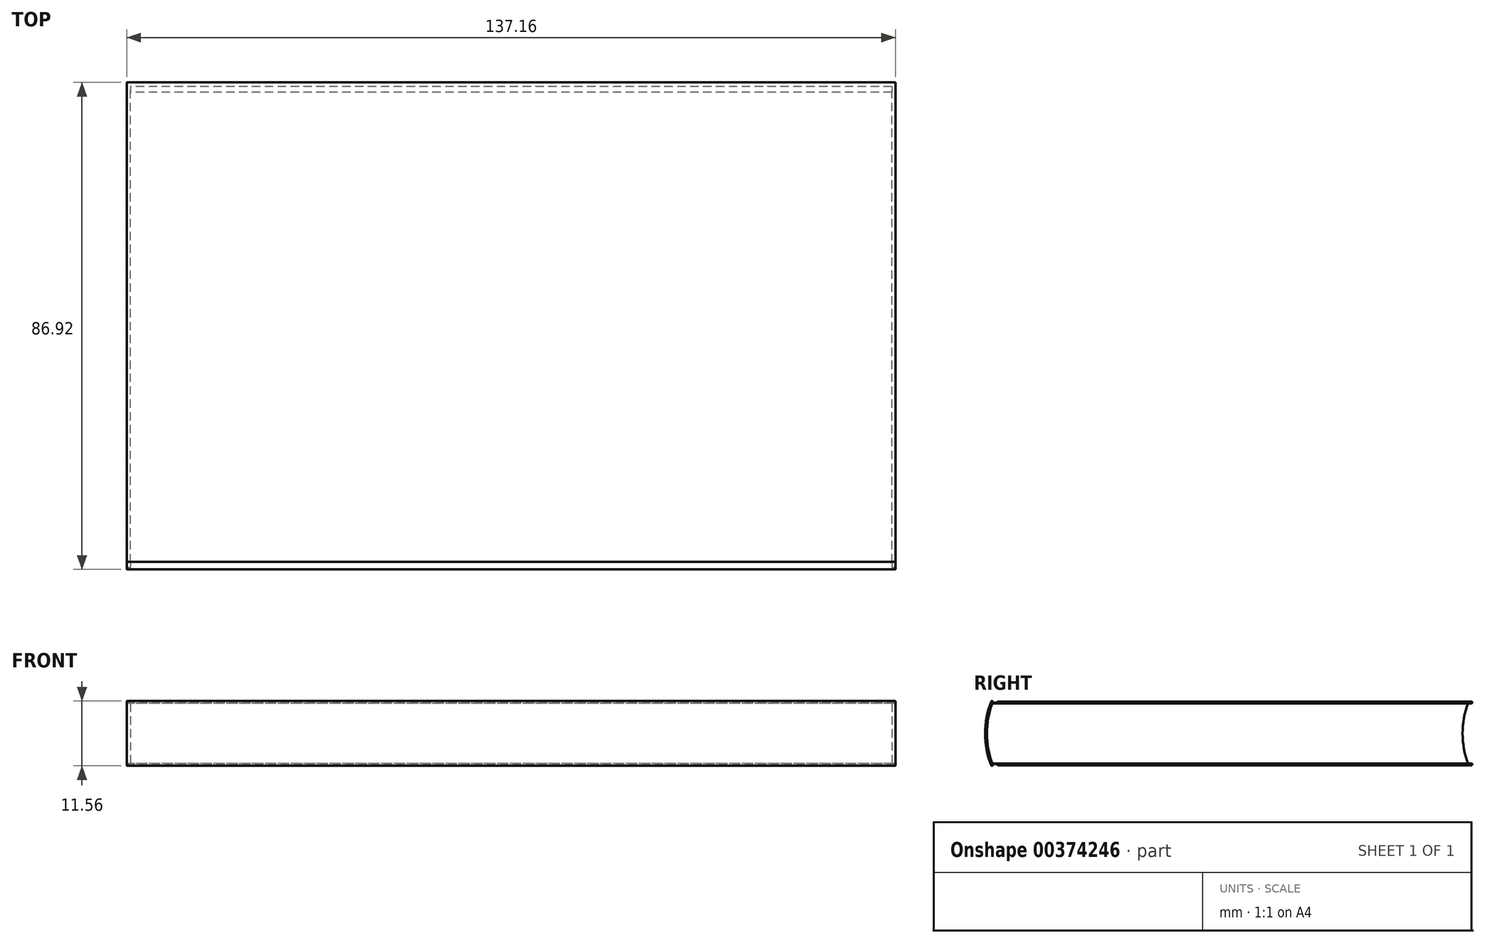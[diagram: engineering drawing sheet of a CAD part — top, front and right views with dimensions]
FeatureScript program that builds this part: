
annotation { "Feature Type Name" : "Feature", "Feature Type Description" : "" }
export const myFeature = defineFeature(function(context is Context, id is Id, definition is map)
    precondition{}
    {
        {
            var Q0;
            Q0=qCreatedBy(makeId("Right.planeOp"),FACE);
            var sketch = newSketch(context, id + "F0", { "sketchPlane" : qUnion([Q0])});
            skLineSegment(sketch, "E0", {"start": v(-62.81, 0) * mm, "end": v(107.73, 0) * mm});
            skArc(sketch, "E1", {"start": v(-62.81, 0) * mm, "mid": v(-63.25, 0.21) * mm, "end": v(-63.7, 0) * mm});
            skArc(sketch, "E2", {"start": v(-64, 0) * mm, "mid": v(-63.85, -0.1) * mm, "end": v(-63.7, 0) * mm});
            skLineSegment(sketch, "E3", {"start": v(-64, 0) * mm, "end": v(-64, 28.97) * mm, "construction": true});
            skLineSegment(sketch, "E4", {"start": v(-64, 28.97) * mm, "end": v(-61.08, 28.97) * mm, "construction": true});
            skLineSegment(sketch, "E5.MirrorCS", {"start": v(-64, 57.95) * mm, "end": v(-64, 28.97) * mm, "construction": true});
            skLineSegment(sketch, "E6.MirrorCS", {"start": v(-62.81, 57.95) * mm, "end": v(107.73, 57.95) * mm});
            skArc(sketch, "E7.MirrorCS", {"start": v(-64, 57.95) * mm, "mid": v(-63.85, 58.05) * mm, "end": v(-63.7, 57.95) * mm});
            skArc(sketch, "E8.MirrorCS", {"start": v(-62.81, 57.95) * mm, "mid": v(-63.25, 57.73) * mm, "end": v(-63.7, 57.95) * mm});
            skArc(sketch, "E9", {"start": v(-64, 57.95) * mm, "mid": v(-69.44, 28.97) * mm, "end": v(-64, 0) * mm});
            skLineSegment(sketch, "E10", {"start": v(-63.85, 0.06) * mm, "end": v(-64, 0) * mm, "construction": true});
            skLineSegment(sketch, "E11", {"start": v(-64, 0) * mm, "end": v(-65.18, 3.02) * mm, "construction": true});
            skLineSegment(sketch, "E12", {"start": v(-64, 0) * mm, "end": v(-63.7, 0) * mm, "construction": true});
            skLineSegment(sketch, "E13", {"start": v(107.73, 0) * mm, "end": v(107.73, 0.31) * mm, "construction": true});
            skArc(sketch, "E14", {"start": v(107.73, 0) * mm, "mid": v(107.89, 0.16) * mm, "end": v(107.73, 0.31) * mm});
            skArc(sketch, "E15.MirrorCS", {"start": v(107.73, 57.95) * mm, "mid": v(107.89, 57.79) * mm, "end": v(107.73, 57.63) * mm});
            skLineSegment(sketch, "E16", {"start": v(107.73, 0.31) * mm, "end": v(-63.8, 0.31) * mm});
            skLineSegment(sketch, "E17", {"start": v(-44.13, 0) * mm, "end": v(-44.13, 0.31) * mm, "construction": true});
            skLineSegment(sketch, "E18", {"start": v(-63.8, 0.31) * mm, "end": v(-64.08, 0.2) * mm, "construction": true});
            skLineSegment(sketch, "E19.MirrorCS", {"start": v(107.73, 57.63) * mm, "end": v(-63.8, 57.63) * mm});
            skArc(sketch, "E20", {"start": v(-63.8, 57.63) * mm, "mid": v(-69.13, 28.97) * mm, "end": v(-63.8, 0.31) * mm});
            skLineSegment(sketch, "E21", {"start": v(-69.13, 28.97) * mm, "end": v(-69.44, 28.97) * mm, "construction": true});
            skLineSegment(sketch, "E22.bottom", {"start": v(-63.8, 57.63) * mm, "end": v(107.2, 57.63) * mm});
            skLineSegment(sketch, "E22.top", {"start": v(-63.8, 0.31) * mm, "end": v(107.2, 0.31) * mm});
            skLineSegment(sketch, "E22.left", {"start": v(-63.8, 57.63) * mm, "end": v(-63.8, 0.31) * mm});
            skLineSegment(sketch, "E22.right", {"start": v(107.2, 57.63) * mm, "end": v(107.2, 0.31) * mm});
            skSolve(sketch);
        }
        {
            var Q0;
            Q0=qCreatedBy(makeId("Right.planeOp"),FACE);
            var sketch = newSketch(context, id + "F1", { "sketchPlane" : qUnion([Q0])});
            skLineSegment(sketch, "E23", {"start": v(-62.81, 0) * mm, "end": v(21.7, 0) * mm});
            skLineSegment(sketch, "E24", {"start": v(-62.81, 0) * mm, "end": v(-62.81, 0) * mm});
            skArc(sketch, "E25", {"start": v(-62.81, 0) * mm, "mid": v(-63.25, 0.21) * mm, "end": v(-63.7, 0) * mm});
            skArc(sketch, "E26", {"start": v(-64, 0) * mm, "mid": v(-63.85, -0.1) * mm, "end": v(-63.7, 0) * mm});
            skLineSegment(sketch, "E27", {"start": v(21.7, 0) * mm, "end": v(21.7, 0) * mm});
            skLineSegment(sketch, "E28", {"start": v(-64, 0) * mm, "end": v(-64, 5.67) * mm, "construction": true});
            skLineSegment(sketch, "E29", {"start": v(-64, 5.67) * mm, "end": v(-60.85, 5.67) * mm, "construction": true});
            skLineSegment(sketch, "E30.MirrorCS", {"start": v(-64, 11.34) * mm, "end": v(-64, 5.67) * mm, "construction": true});
            skArc(sketch, "E31.MirrorCS", {"start": v(-64, 11.34) * mm, "mid": v(-63.85, 11.45) * mm, "end": v(-63.7, 11.34) * mm});
            skArc(sketch, "E32.MirrorCS", {"start": v(-62.81, 11.34) * mm, "mid": v(-63.25, 11.13) * mm, "end": v(-63.7, 11.34) * mm});
            skLineSegment(sketch, "E33.MirrorCS", {"start": v(-62.81, 11.34) * mm, "end": v(21.7, 11.34) * mm});
            skLineSegment(sketch, "E34.MirrorCS", {"start": v(21.7, 11.34) * mm, "end": v(21.7, 11.34) * mm});
            skLineSegment(sketch, "E35.0", {"start": v(-64, 0) * mm, "end": v(-65.18, 3.02) * mm, "construction": true});
            skArc(sketch, "E36", {"start": v(-64, 11.34) * mm, "mid": v(-65.07, 5.67) * mm, "end": v(-64, 0) * mm});
            skArc(sketch, "E37", {"start": v(-63.8, 11.03) * mm, "mid": v(-64.77, 5.67) * mm, "end": v(-63.8, 0.31) * mm});
            skLineSegment(sketch, "E38", {"start": v(-64.77, 5.67) * mm, "end": v(-65.07, 5.67) * mm, "construction": true});
            skLineSegment(sketch, "E39", {"start": v(-64.06, 1) * mm, "end": v(-63.8, 0.31) * mm, "construction": true});
            skLineSegment(sketch, "E40", {"start": v(-64, 0) * mm, "end": v(-63.72, 0.1) * mm, "construction": true});
            skLineSegment(sketch, "E41", {"start": v(21.7, 0.31) * mm, "end": v(21.7, 0) * mm, "construction": true});
            skArc(sketch, "E42", {"start": v(21.7, 0) * mm, "mid": v(21.85, 0.16) * mm, "end": v(21.7, 0.31) * mm});
            skLineSegment(sketch, "E43", {"start": v(-63.8, 0.31) * mm, "end": v(21.7, 0.31) * mm});
            skLineSegment(sketch, "E44.MirrorCS", {"start": v(-63.8, 11.03) * mm, "end": v(21.7, 11.03) * mm});
            skArc(sketch, "E45.MirrorCS", {"start": v(21.7, 11.34) * mm, "mid": v(21.85, 11.19) * mm, "end": v(21.7, 11.03) * mm});
            skLineSegment(sketch, "E46", {"start": v(-63.8, 11.03) * mm, "end": v(-63.8, 0.31) * mm, "construction": true});
            skLineSegment(sketch, "E47", {"start": v(-63.8, 5.67) * mm, "end": v(-64.77, 5.67) * mm, "construction": true});
            skLineSegment(sketch, "E48", {"start": v(21.09, 11.03) * mm, "end": v(21.09, 0.31) * mm, "construction": true});
            skLineSegment(sketch, "E49", {"start": v(21.09, 5.67) * mm, "end": v(20.12, 5.67) * mm, "construction": true});
            skArc(sketch, "E50", {"start": v(21.09, 11.03) * mm, "mid": v(20.12, 5.67) * mm, "end": v(21.09, 0.31) * mm});
            skSolve(sketch);
        }
        {
            var Q0;
            Q0=makeQuery(id+"F1.imprint","IMPRINT",FACE,{"disambiguationData":[TD([[makeQuery(id+"F1.imprint","IMPRINT",EDGE,{"derivedFrom":sQuery(id+"F1.wireOp",EDGE,"E23")}),1.0]])]});
            extrude(context, id + "F2", {"entities" : qUnion([Q0]), "endBound" : BoundingType.SYMMETRIC, "depth" : 137.16 * mm});
        }
        {
            var Q0;
            Q0=makeQuery(id+"F2.opExtrude","CAP_EDGE",EDGE,{"disambiguationData":[OSD([sQuery(id+"F1.wireOp",EDGE,"E36")])],"isStart":false});
            var Q1;
            Q1=makeQuery(id+"F2.opExtrude","CAP_EDGE",EDGE,{"disambiguationData":[OSD([sQuery(id+"F1.wireOp",EDGE,"E37")])],"isStart":false});
            var Q2;
            Q2=makeQuery(id+"F2.opExtrude","CAP_EDGE",EDGE,{"disambiguationData":[OSD([sQuery(id+"F1.wireOp",EDGE,"E31.MirrorCS")])],"isStart":false});
            var Q3;
            Q3=makeQuery(id+"F2.opExtrude","CAP_EDGE",EDGE,{"disambiguationData":[OSD([sQuery(id+"F1.wireOp",EDGE,"E32.MirrorCS")])],"isStart":false});
            var Q4;
            Q4=makeQuery(id+"F2.opExtrude","CAP_EDGE",EDGE,{"disambiguationData":[OSD([sQuery(id+"F1.wireOp",EDGE,"142f4ce0-e9b1-4b00-a699-831a67d240180.MirrorCS"),sQuery(id+"F1.wireOp",EDGE,"xczyOIpz-feBP-V8Je-0c5D-2grpSOWJgWFw.top")])],"isStart":false});
            var Q5;
            Q5=makeQuery(id+"F2.opExtrude","CAP_EDGE",EDGE,{"disambiguationData":[OSD([sQuery(id+"F1.wireOp",EDGE,"E33.MirrorCS")])],"isStart":false});
            var Q6;
            Q6=makeQuery(id+"F2.opExtrude","CAP_EDGE",EDGE,{"disambiguationData":[OSD([sQuery(id+"F1.wireOp",EDGE,"E34.MirrorCS")])],"isStart":false});
            var Q7;
            Q7=makeQuery(id+"F2.opExtrude","CAP_EDGE",EDGE,{"disambiguationData":[OSD([sQuery(id+"F1.wireOp",EDGE,"E26")])],"isStart":false});
            var Q8;
            Q8=makeQuery(id+"F2.opExtrude","CAP_EDGE",EDGE,{"disambiguationData":[OSD([sQuery(id+"F1.wireOp",EDGE,"E25")])],"isStart":false});
            var Q9;
            Q9=makeQuery(id+"F2.opExtrude","CAP_EDGE",EDGE,{"disambiguationData":[OSD([sQuery(id+"F1.wireOp",EDGE,"E23")])],"isStart":false});
            var Q10;
            Q10=makeQuery(id+"F2.opExtrude","CAP_EDGE",EDGE,{"disambiguationData":[OSD([sQuery(id+"F1.wireOp",EDGE,"r9oz5I4B-ejXC-MW1O-M8zh-qOg59PADHznW"),sQuery(id+"F1.wireOp",EDGE,"xczyOIpz-feBP-V8Je-0c5D-2grpSOWJgWFw.bottom")])],"isStart":false});
            var Q11;
            Q11=makeQuery(id+"F2.opExtrude","CAP_EDGE",EDGE,{"disambiguationData":[OSD([sQuery(id+"F1.wireOp",EDGE,"E27")])],"isStart":false});
            fillet(context, id + "F3", {"entities" : qUnion([Q0, Q1, Q2, Q3, Q4, Q5, Q6, Q7, Q8, Q9, Q10, Q11]), "radius" : 0.06 * mm, "tangentPropagation" : true, "allowEdgeOverflow" : false});
        }
        {
            var Q0;
            Q0=makeQuery(id+"F2.opExtrude","CAP_EDGE",EDGE,{"disambiguationData":[OSD([sQuery(id+"F1.wireOp",EDGE,"E34.MirrorCS")])],"isStart":true});
            var Q1;
            Q1=makeQuery(id+"F2.opExtrude","CAP_EDGE",EDGE,{"disambiguationData":[OSD([sQuery(id+"F1.wireOp",EDGE,"E33.MirrorCS")])],"isStart":true});
            var Q2;
            Q2=makeQuery(id+"F2.opExtrude","CAP_EDGE",EDGE,{"disambiguationData":[OSD([sQuery(id+"F1.wireOp",EDGE,"142f4ce0-e9b1-4b00-a699-831a67d240180.MirrorCS"),sQuery(id+"F1.wireOp",EDGE,"xczyOIpz-feBP-V8Je-0c5D-2grpSOWJgWFw.top")])],"isStart":true});
            var Q3;
            Q3=makeQuery(id+"F2.opExtrude","CAP_EDGE",EDGE,{"disambiguationData":[OSD([sQuery(id+"F1.wireOp",EDGE,"E32.MirrorCS")])],"isStart":true});
            var Q4;
            Q4=makeQuery(id+"F2.opExtrude","CAP_EDGE",EDGE,{"disambiguationData":[OSD([sQuery(id+"F1.wireOp",EDGE,"E31.MirrorCS")])],"isStart":true});
            var Q5;
            Q5=makeQuery(id+"F2.opExtrude","CAP_EDGE",EDGE,{"disambiguationData":[OSD([sQuery(id+"F1.wireOp",EDGE,"E36")])],"isStart":true});
            var Q6;
            Q6=makeQuery(id+"F2.opExtrude","CAP_EDGE",EDGE,{"disambiguationData":[OSD([sQuery(id+"F1.wireOp",EDGE,"E37")])],"isStart":true});
            var Q7;
            Q7=makeQuery(id+"F2.opExtrude","CAP_EDGE",EDGE,{"disambiguationData":[OSD([sQuery(id+"F1.wireOp",EDGE,"E26")])],"isStart":true});
            var Q8;
            Q8=makeQuery(id+"F2.opExtrude","CAP_EDGE",EDGE,{"disambiguationData":[OSD([sQuery(id+"F1.wireOp",EDGE,"E25")])],"isStart":true});
            var Q9;
            Q9=makeQuery(id+"F2.opExtrude","CAP_EDGE",EDGE,{"disambiguationData":[OSD([sQuery(id+"F1.wireOp",EDGE,"r9oz5I4B-ejXC-MW1O-M8zh-qOg59PADHznW"),sQuery(id+"F1.wireOp",EDGE,"xczyOIpz-feBP-V8Je-0c5D-2grpSOWJgWFw.bottom")])],"isStart":true});
            var Q10;
            Q10=makeQuery(id+"F2.opExtrude","CAP_EDGE",EDGE,{"disambiguationData":[OSD([sQuery(id+"F1.wireOp",EDGE,"E23")])],"isStart":true});
            var Q11;
            Q11=makeQuery(id+"F2.opExtrude","CAP_EDGE",EDGE,{"disambiguationData":[OSD([sQuery(id+"F1.wireOp",EDGE,"E27")])],"isStart":true});
            fillet(context, id + "F4", {"entities" : qUnion([Q0, Q1, Q2, Q3, Q4, Q5, Q6, Q7, Q8, Q9, Q10, Q11]), "radius" : 0.06 * mm, "tangentPropagation" : true, "allowEdgeOverflow" : false});
        }
        {
            var Q0;
            Q0=makeQuery(id+"F2.opExtrude","SWEPT_EDGE",EDGE,{"disambiguationData":[OSD([sQuery(id+"F1.wireOp",EDGE,"E32.MirrorCS"),sQuery(id+"F1.wireOp",EDGE,"E33.MirrorCS")])]});
            var Q1;
            Q1=makeQuery(id+"F4.opFillet","BLEND_EDGE",EDGE,{"blendedFrom":[makeQuery(id+"F2.opExtrude","CAP_EDGE",EDGE,{"disambiguationData":[OSD([sQuery(id+"F1.wireOp",EDGE,"E32.MirrorCS")])],"isStart":true}),makeQuery(id+"F2.opExtrude","CAP_EDGE",EDGE,{"disambiguationData":[OSD([sQuery(id+"F1.wireOp",EDGE,"E33.MirrorCS")])],"isStart":true})],"blendedInto":[]});
            var Q2;
            Q2=makeQuery(id+"F3.opFillet","BLEND_EDGE",EDGE,{"blendedFrom":[makeQuery(id+"F2.opExtrude","CAP_EDGE",EDGE,{"disambiguationData":[OSD([sQuery(id+"F1.wireOp",EDGE,"E32.MirrorCS")])],"isStart":false}),makeQuery(id+"F2.opExtrude","CAP_EDGE",EDGE,{"disambiguationData":[OSD([sQuery(id+"F1.wireOp",EDGE,"E33.MirrorCS")])],"isStart":false})],"blendedInto":[]});
            var Q3;
            Q3=makeQuery(id+"F2.opExtrude","SWEPT_EDGE",EDGE,{"disambiguationData":[OSD([sQuery(id+"F1.wireOp",EDGE,"E23"),sQuery(id+"F1.wireOp",EDGE,"E25")])]});
            var Q4;
            Q4=makeQuery(id+"F3.opFillet","BLEND_EDGE",EDGE,{"blendedFrom":[makeQuery(id+"F2.opExtrude","CAP_EDGE",EDGE,{"disambiguationData":[OSD([sQuery(id+"F1.wireOp",EDGE,"E23")])],"isStart":false}),makeQuery(id+"F2.opExtrude","CAP_EDGE",EDGE,{"disambiguationData":[OSD([sQuery(id+"F1.wireOp",EDGE,"E25")])],"isStart":false})],"blendedInto":[]});
            var Q5;
            Q5=makeQuery(id+"F4.opFillet","BLEND_EDGE",EDGE,{"blendedFrom":[makeQuery(id+"F2.opExtrude","CAP_EDGE",EDGE,{"disambiguationData":[OSD([sQuery(id+"F1.wireOp",EDGE,"E23")])],"isStart":true}),makeQuery(id+"F2.opExtrude","CAP_EDGE",EDGE,{"disambiguationData":[OSD([sQuery(id+"F1.wireOp",EDGE,"E25")])],"isStart":true})],"blendedInto":[]});
            fillet(context, id + "F5", {"entities" : qUnion([Q0, Q1, Q2, Q3, Q4, Q5]), "radius" : 0.13 * mm, "tangentPropagation" : true, "allowEdgeOverflow" : false});
        }
        {
            var Q0;
            {var subQ0=sQuery(id+"F1.wireOp",EDGE,"E37");Q0=makeQuery(id+"F1.imprint","IMPRINT",FACE,{"disambiguationData":[TD([[makeQuery(id+"F1.imprint","IMPRINT",EDGE,{"derivedFrom":subQ0}),1.0]])]});}
            extrude(context, id + "F6", {"entities" : qUnion([Q0]), "operationType" : NewBodyOperationType.ADD, "endBound" : BoundingType.SYMMETRIC, "depth" : 135.89 * mm});
        }
    });
